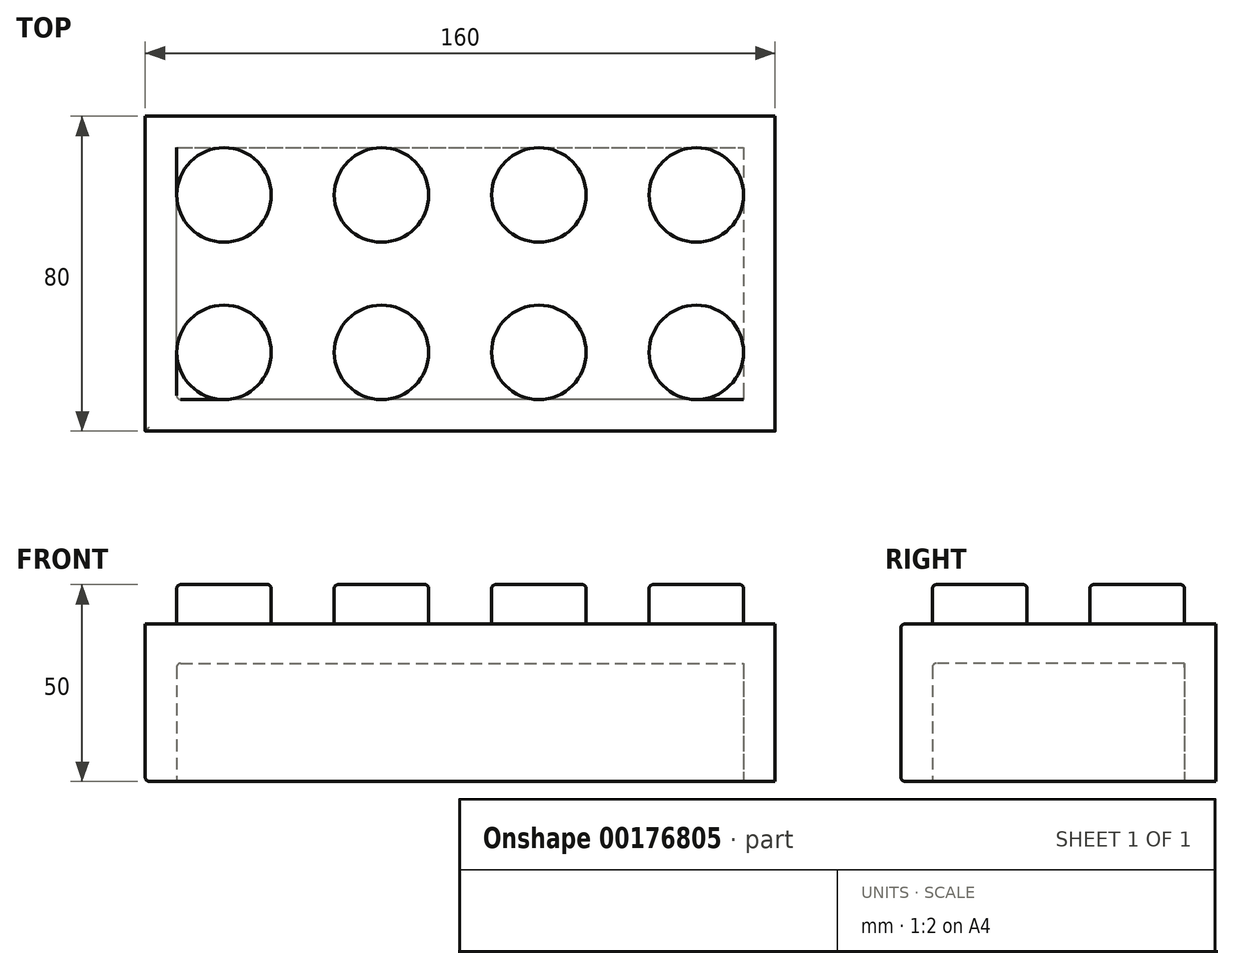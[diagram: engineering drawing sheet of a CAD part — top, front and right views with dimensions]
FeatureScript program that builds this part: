
annotation { "Feature Type Name" : "Feature", "Feature Type Description" : "" }
export const myFeature = defineFeature(function(context is Context, id is Id, definition is map)
    precondition{}
    {
        {
            var Q0;
            Q0=qCreatedBy(makeId("Top.planeOp"),FACE);
            var sketch = newSketch(context, id + "F0", { "sketchPlane" : qUnion([Q0])});
            skLineSegment(sketch, "E0.bottom", {"start": v(-70.6, 55.3) * mm, "end": v(89.4, 55.3) * mm});
            skLineSegment(sketch, "E0.top", {"start": v(-70.6, -24.7) * mm, "end": v(89.4, -24.7) * mm});
            skLineSegment(sketch, "E0.left", {"start": v(-70.6, 55.3) * mm, "end": v(-70.6, -24.7) * mm});
            skLineSegment(sketch, "E0.right", {"start": v(89.4, 55.3) * mm, "end": v(89.4, -24.7) * mm});
            skSolve(sketch);
        }
        {
            var Q0;
            Q0=qSketchRegion(id+"F0",true);
            extrude(context, id + "F1", {"entities" : qUnion([Q0]), "depth" : 40 * mm});
        }
        {
            var Q0;
            Q0=makeQuery(id+"F1.opExtrude","CAP_FACE",FACE,{"disambiguationData":[OSD([sQuery(id+"F0.wireOp",EDGE,"E0.bottom"),sQuery(id+"F0.wireOp",EDGE,"E0.top"),sQuery(id+"F0.wireOp",EDGE,"E0.left"),sQuery(id+"F0.wireOp",EDGE,"E0.right")])],"isStart":true});
            var sketch = newSketch(context, id + "F2", { "sketchPlane" : qUnion([Q0])});
            skLineSegment(sketch, "E1.0", {"start": v(-62.6, -47.3) * mm, "end": v(81.4, -47.3) * mm});
            skLineSegment(sketch, "E1.1", {"start": v(-62.6, 16.7) * mm, "end": v(-62.6, -47.3) * mm});
            skLineSegment(sketch, "E1.2", {"start": v(81.4, 16.7) * mm, "end": v(-62.6, 16.7) * mm});
            skLineSegment(sketch, "E1.3", {"start": v(81.4, -47.3) * mm, "end": v(81.4, 16.7) * mm});
            skSolve(sketch);
        }
        {
            var Q0;
            Q0=qSketchRegion(id+"F2",true);
            extrude(context, id + "F3", {"entities" : qUnion([Q0]), "operationType" : NewBodyOperationType.REMOVE, "oppositeDirection" : true, "depth" : 30 * mm});
        }
        {
            var Q0;
            Q0=makeQuery(id+"F1.opExtrude","CAP_FACE",FACE,{"disambiguationData":[OSD([sQuery(id+"F0.wireOp",EDGE,"E0.bottom"),sQuery(id+"F0.wireOp",EDGE,"E0.top"),sQuery(id+"F0.wireOp",EDGE,"E0.left"),sQuery(id+"F0.wireOp",EDGE,"E0.right")])],"isStart":false});
            var sketch = newSketch(context, id + "F4", { "sketchPlane" : qUnion([Q0])});
            skCircle(sketch, "E2", {"center": v(-50.6, 35.3) * mm, "radius": 12 * mm});
            skCircle(sketch, "E3.0.1.0", {"center": v(-50.6, -4.7) * mm, "radius": 12 * mm});
            skCircle(sketch, "E3.1.0.0", {"center": v(-10.6, 35.3) * mm, "radius": 12 * mm});
            skCircle(sketch, "E3.1.1.0", {"center": v(-10.6, -4.7) * mm, "radius": 12 * mm});
            skCircle(sketch, "E3.2.0.0", {"center": v(29.4, 35.3) * mm, "radius": 12 * mm});
            skCircle(sketch, "E3.2.1.0", {"center": v(29.4, -4.7) * mm, "radius": 12 * mm});
            skCircle(sketch, "E3.3.0.0", {"center": v(69.4, 35.3) * mm, "radius": 12 * mm});
            skCircle(sketch, "E3.3.1.0", {"center": v(69.4, -4.7) * mm, "radius": 12 * mm});
            skLineSegment(sketch, "E3.direction1", {"start": v(-50.6, 35.3) * mm, "end": v(-10.6, 35.3) * mm, "construction": true});
            skLineSegment(sketch, "E3.direction2", {"start": v(-50.6, 35.3) * mm, "end": v(-50.6, -4.7) * mm, "construction": true});
            skSolve(sketch);
        }
        {
            var Q0;
            Q0=qSketchRegion(id+"F4",true);
            var Q1;
            Q1=qConstructionFilter(qBodyType(qCreatedBy(id+"F4",EDGE),BodyType.WIRE),ConstructionObject.NO);
            extrude(context, id + "F5", {"entities" : qUnion([Q0]), "operationType" : NewBodyOperationType.ADD, "surfaceEntities" : qUnion([Q1]), "depth" : 10 * mm});
        }
        {
            var Q0;
            Q0=makeQuery(id+"F5.opExtrude","CAP_FACE",FACE,{"disambiguationData":[OSD([sQuery(id+"F4.wireOp",EDGE,"E3.0.1.0")])],"isStart":false});
            var Q1;
            Q1=makeQuery(id+"F5.opExtrude","CAP_FACE",FACE,{"disambiguationData":[OSD([sQuery(id+"F4.wireOp",EDGE,"E2")])],"isStart":false});
            var Q2;
            Q2=makeQuery(id+"F5.opExtrude","CAP_FACE",FACE,{"disambiguationData":[OSD([sQuery(id+"F4.wireOp",EDGE,"E3.1.0.0")])],"isStart":false});
            var Q3;
            Q3=makeQuery(id+"F5.opExtrude","CAP_FACE",FACE,{"disambiguationData":[OSD([sQuery(id+"F4.wireOp",EDGE,"E3.1.1.0")])],"isStart":false});
            var Q4;
            Q4=makeQuery(id+"F1.opExtrude","CAP_EDGE",EDGE,{"disambiguationData":[OSD([sQuery(id+"F0.wireOp",EDGE,"E0.top")])],"isStart":true});
            var Q5;
            Q5=makeQuery(id+"F1.opExtrude","CAP_EDGE",EDGE,{"disambiguationData":[OSD([sQuery(id+"F0.wireOp",EDGE,"E0.top")])],"isStart":false});
            var Q6;
            Q6=makeQuery(id+"F3.boolean.opBoolean","COPY",EDGE,{"derivedFrom":makeQuery(id+"F3.opExtrude","SWEPT_EDGE",EDGE,{"disambiguationData":[OSD([sQuery(id+"F2.wireOp",EDGE,"E1.1"),sQuery(id+"F2.wireOp",EDGE,"E1.2")])]})});
            var Q7;
            Q7=makeQuery(id+"F3.boolean.opBoolean","COPY",EDGE,{"derivedFrom":makeQuery(id+"F3.opExtrude","CAP_EDGE",EDGE,{"disambiguationData":[OSD([sQuery(id+"F2.wireOp",EDGE,"E1.1")])],"isStart":false})});
            var Q8;
            Q8=makeQuery(id+"F3.boolean.opBoolean","COPY",EDGE,{"derivedFrom":makeQuery(id+"F3.opExtrude","CAP_EDGE",EDGE,{"disambiguationData":[OSD([sQuery(id+"F2.wireOp",EDGE,"E1.2")])],"isStart":false})});
            var Q9;
            Q9=makeQuery(id+"F1.opExtrude","CAP_EDGE",EDGE,{"disambiguationData":[OSD([sQuery(id+"F0.wireOp",EDGE,"E0.left")])],"isStart":true});
            var Q10;
            Q10=makeQuery(id+"F3.boolean.opBoolean","COPY",EDGE,{"derivedFrom":makeQuery(id+"F3.opExtrude","CAP_EDGE",EDGE,{"disambiguationData":[OSD([sQuery(id+"F2.wireOp",EDGE,"E1.1")])],"isStart":true})});
            var Q11;
            Q11=makeQuery(id+"F3.boolean.opBoolean","COPY",EDGE,{"derivedFrom":makeQuery(id+"F3.opExtrude","CAP_EDGE",EDGE,{"disambiguationData":[OSD([sQuery(id+"F2.wireOp",EDGE,"E1.2")])],"isStart":true})});
            var Q12;
            Q12=makeQuery(id+"F5.opExtrude","CAP_FACE",FACE,{"disambiguationData":[OSD([sQuery(id+"F4.wireOp",EDGE,"E3.2.1.0")])],"isStart":false});
            var Q13;
            Q13=makeQuery(id+"F5.opExtrude","CAP_FACE",FACE,{"disambiguationData":[OSD([sQuery(id+"F4.wireOp",EDGE,"E3.0.1.0")])],"isStart":false});
            var Q14;
            Q14=makeQuery(id+"F5.opExtrude","CAP_FACE",FACE,{"disambiguationData":[OSD([sQuery(id+"F4.wireOp",EDGE,"E2")])],"isStart":false});
            var Q15;
            Q15=makeQuery(id+"F5.opExtrude","CAP_FACE",FACE,{"disambiguationData":[OSD([sQuery(id+"F4.wireOp",EDGE,"E3.1.0.0")])],"isStart":false});
            var Q16;
            Q16=makeQuery(id+"F5.opExtrude","CAP_FACE",FACE,{"disambiguationData":[OSD([sQuery(id+"F4.wireOp",EDGE,"E3.1.1.0")])],"isStart":false});
            var Q17;
            Q17=makeQuery(id+"F5.opExtrude","CAP_FACE",FACE,{"disambiguationData":[OSD([sQuery(id+"F4.wireOp",EDGE,"E3.2.1.0")])],"isStart":false});
            var Q18;
            Q18=makeQuery(id+"F5.opExtrude","CAP_FACE",FACE,{"disambiguationData":[OSD([sQuery(id+"F4.wireOp",EDGE,"E3.3.1.0")])],"isStart":false});
            var Q19;
            Q19=makeQuery(id+"F5.opExtrude","CAP_FACE",FACE,{"disambiguationData":[OSD([sQuery(id+"F4.wireOp",EDGE,"E3.3.0.0")])],"isStart":false});
            var Q20;
            Q20=makeQuery(id+"F5.opExtrude","CAP_FACE",FACE,{"disambiguationData":[OSD([sQuery(id+"F4.wireOp",EDGE,"E3.2.0.0")])],"isStart":false});
            fillet(context, id + "F6", {"entities" : qUnion([Q0, Q1, Q2, Q3, Q4, Q5, Q6, Q7, Q8, Q9, Q10, Q11, Q12, Q13, Q14, Q15, Q16, Q17, Q18, Q19, Q20]), "radius" : 1 * mm, "tangentPropagation" : true, "allowEdgeOverflow" : false});
        }
    });
